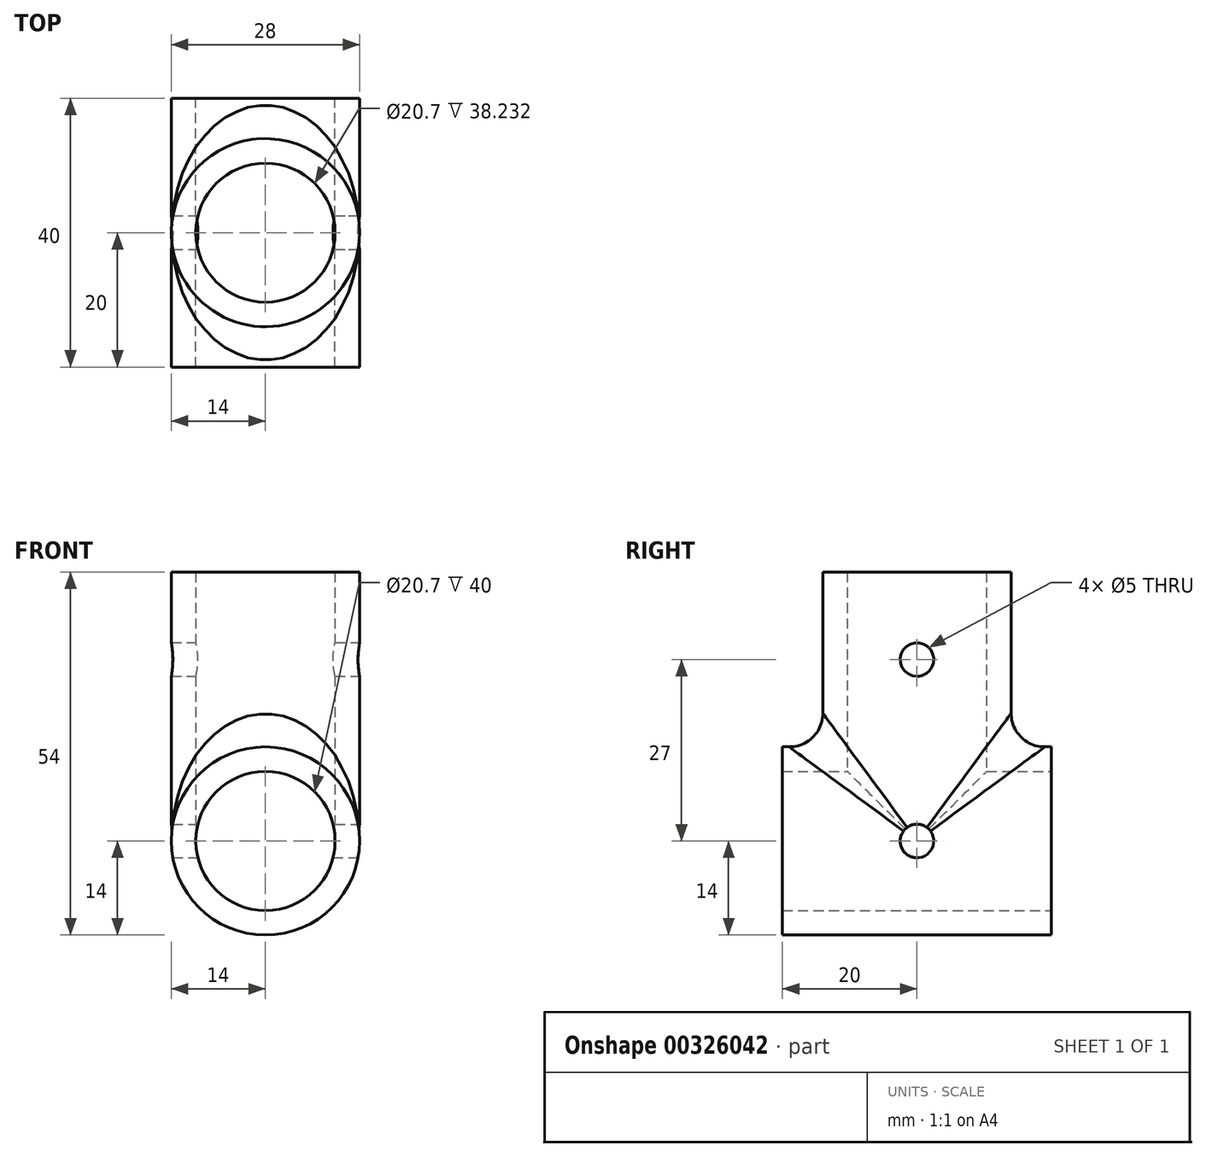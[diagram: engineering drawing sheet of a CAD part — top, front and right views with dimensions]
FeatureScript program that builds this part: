
annotation { "Feature Type Name" : "Feature", "Feature Type Description" : "" }
export const myFeature = defineFeature(function(context is Context, id is Id, definition is map)
    precondition{}
    {
        {
            var Q0;
            Q0=qCreatedBy(makeId("Front.planeOp"),FACE);
            var sketch = newSketch(context, id + "F0", { "sketchPlane" : qUnion([Q0])});
            skCircle(sketch, "E0", {"center": v(0, 0) * mm, "radius": 14 * mm});
            skSolve(sketch);
        }
        {
            var Q0;
            Q0=makeQuery(id+"F0.imprint","IMPRINT",FACE,{"disambiguationData":[TD([[makeQuery(id+"F0.imprint","IMPRINT",EDGE,{"derivedFrom":sQuery(id+"F0.wireOp",EDGE,"E0")}),1.0]])]});
            extrude(context, id + "F1", {"entities" : qUnion([Q0]), "depth" : 20 * mm, "hasSecondDirection" : true, "secondDirectionOppositeDirection" : true, "secondDirectionDepth" : 20 * mm});
        }
        {
            var Q0;
            Q0=qCreatedBy(makeId("Top.planeOp"),FACE);
            var sketch = newSketch(context, id + "F2", { "sketchPlane" : qUnion([Q0])});
            skCircle(sketch, "E1", {"center": v(0, 0) * mm, "radius": 14 * mm});
            skSolve(sketch);
        }
        {
            var Q0;
            Q0=makeQuery(id+"F2.imprint","IMPRINT",FACE,{"disambiguationData":[TD([[makeQuery(id+"F2.imprint","IMPRINT",EDGE,{"derivedFrom":sQuery(id+"F2.wireOp",EDGE,"E1")}),1.0]])]});
            extrude(context, id + "F3", {"entities" : qUnion([Q0]), "operationType" : NewBodyOperationType.ADD, "depth" : 40 * mm});
        }
        {
            var Q0;
            Q0=makeQuery(id+"F1.opExtrude","CAP_FACE",FACE,{"disambiguationData":[OSD([sQuery(id+"F0.wireOp",EDGE,"E0")])],"isStart":false});
            var sketch = newSketch(context, id + "F4", { "sketchPlane" : qUnion([Q0])});
            skPoint(sketch, "E2.0", {"position": v(0, 0) * mm});
            skSolve(sketch);
        }
        {
            var Q0;
            Q0=makeQuery(id+"F3.opExtrude","CAP_FACE",FACE,{"disambiguationData":[OSD([sQuery(id+"F2.wireOp",EDGE,"E1")])],"isStart":false});
            var sketch = newSketch(context, id + "F5", { "sketchPlane" : qUnion([Q0])});
            skPoint(sketch, "E3.0", {"position": v(0, 0) * mm});
            skSolve(sketch);
        }
        {
            var Q0;
            Q0=sQuery(id+"F24hy0gCMbYL9Hx_1.wireOp",VERTEX,"e79b2ffc-b069-4af7-8da4-9cec6bc6b9a4.0");
            var Q1;
            Q1=sQuery(id+"F4.wireOp",VERTEX,"E2.0");
            var Q2;
            Q2=sQuery(id+"F5.wireOp",VERTEX,"E3.0");
            var Q3;
            Q3=makeQuery(id+"F1.opExtrude","SWEPT_BODY",BODY,{"disambiguationData":[OSD([sQuery(id+"F0.wireOp",EDGE,"E0")])]});
            hole(context, id + "F6", {"style" : HoleStyle.SIMPLE, "endStyle" : HoleEndStyle.BLIND, "holeDiameter" : 20.7 * mm, "holeDepth" : 40 * mm, "tappedDepth" : 12 * mm, "tapClearance" : 3, "locations" : qUnion([Q0, Q1, Q2]), "scope" : qUnion([Q3]), "startStyle" : HoleStartStyle.PART});
        }
        {
            var Q0;
            Q0=makeQuery(id+"FaHmLC6Gn3Dgabr_1.boolean.opBoolean","INTERSECT",EDGE,{"derivedFrom":[makeQuery(id+"F3.opExtrude","SWEPT_FACE",FACE,{"disambiguationData":[OSD([sQuery(id+"F2.wireOp",EDGE,"E1")])]}),makeQuery(id+"FaHmLC6Gn3Dgabr_1.opExtrude","SWEPT_FACE",FACE,{"disambiguationData":[OSD([sQuery(id+"FM3x9xQwSGay4u9_1.wireOp",EDGE,"9ACyZtps-vr8r-rKMI-yhLd-u2BAxOoJ523N")])]})]});
            var Q1;
            Q1=makeQuery(id+"FaHmLC6Gn3Dgabr_1.boolean.opBoolean","INTERSECT",EDGE,{"derivedFrom":[makeQuery(id+"F1.opExtrude","SWEPT_FACE",FACE,{"disambiguationData":[OSD([sQuery(id+"F0.wireOp",EDGE,"E0")])]}),makeQuery(id+"FaHmLC6Gn3Dgabr_1.opExtrude","SWEPT_FACE",FACE,{"disambiguationData":[OSD([sQuery(id+"FM3x9xQwSGay4u9_1.wireOp",EDGE,"9ACyZtps-vr8r-rKMI-yhLd-u2BAxOoJ523N")])]})]});
            var Q2;
            Q2=makeQuery(id+"F3.boolean.opBoolean","INTERSECT",EDGE,{"derivedFrom":[makeQuery(id+"F1.opExtrude","SWEPT_FACE",FACE,{"disambiguationData":[OSD([sQuery(id+"F0.wireOp",EDGE,"E0")])]}),makeQuery(id+"F3.opExtrude","SWEPT_FACE",FACE,{"disambiguationData":[OSD([sQuery(id+"F2.wireOp",EDGE,"E1")])]})]});
            fillet(context, id + "F7", {"entities" : qUnion([Q0, Q1, Q2]), "radius" : 5 * mm, "tangentPropagation" : true, "allowEdgeOverflow" : false});
        }
        {
            var Q0;
            Q0=qCreatedBy(makeId("Right.planeOp"),FACE);
            cPlane(context, id + "F8", {"entities" : qUnion([Q0]), "cplaneType" : CPlaneType.OFFSET, "offset" : 25 * mm, "oppositeDirection" : true, "width" : 150 * mm, "height" : 150 * mm});
        }
        {
            var Q0;
            Q0=qCreatedBy(id+"F8.planeOp",FACE);
            var sketch = newSketch(context, id + "F9", { "sketchPlane" : qUnion([Q0])});
            skLineSegment(sketch, "E4.0", {"start": v(-14, 40) * mm, "end": v(14, 40) * mm});
            skLineSegment(sketch, "E5.0", {"start": v(-20, -14) * mm, "end": v(-20, 14) * mm});
            skPoint(sketch, "E6", {"position": v(0, 27) * mm});
            skPoint(sketch, "E6.positionSnap0", {"position": v(0, 40) * mm});
            skPoint(sketch, "E7", {"position": v(0, 0) * mm});
            skPoint(sketch, "E7.positionSnap0", {"position": v(-20, 0) * mm});
            skCircle(sketch, "E8.0", {"center": v(0, 0) * mm, "radius": 14 * mm, "construction": true});
            skLineSegment(sketch, "E9", {"start": v(0, 40) * mm, "end": v(0, 14) * mm, "construction": true});
            skSolve(sketch);
        }
        {
            var Q0;
            Q0=sQuery(id+"F6LFL7wuMSnmu2D_1.wireOp",VERTEX,"968162a3-0b9f-4b82-9a42-acb8d730a663");
            var Q1;
            Q1=sQuery(id+"F9.wireOp",VERTEX,"E6");
            var Q2;
            Q2=sQuery(id+"F9.wireOp",VERTEX,"E7");
            var Q3;
            Q3=makeQuery(id+"F1.opExtrude","SWEPT_BODY",BODY,{"disambiguationData":[OSD([sQuery(id+"F0.wireOp",EDGE,"E0")])]});
            hole(context, id + "F10", {"style" : HoleStyle.SIMPLE, "endStyle" : HoleEndStyle.BLIND, "oppositeDirection" : true, "holeDiameter" : 5 * mm, "holeDepth" : 30 * mm, "tappedDepth" : 12 * mm, "tapClearance" : 3, "locations" : qUnion([Q0, Q1, Q2]), "scope" : qUnion([Q3]), "startStyle" : HoleStartStyle.PART});
        }
    });
